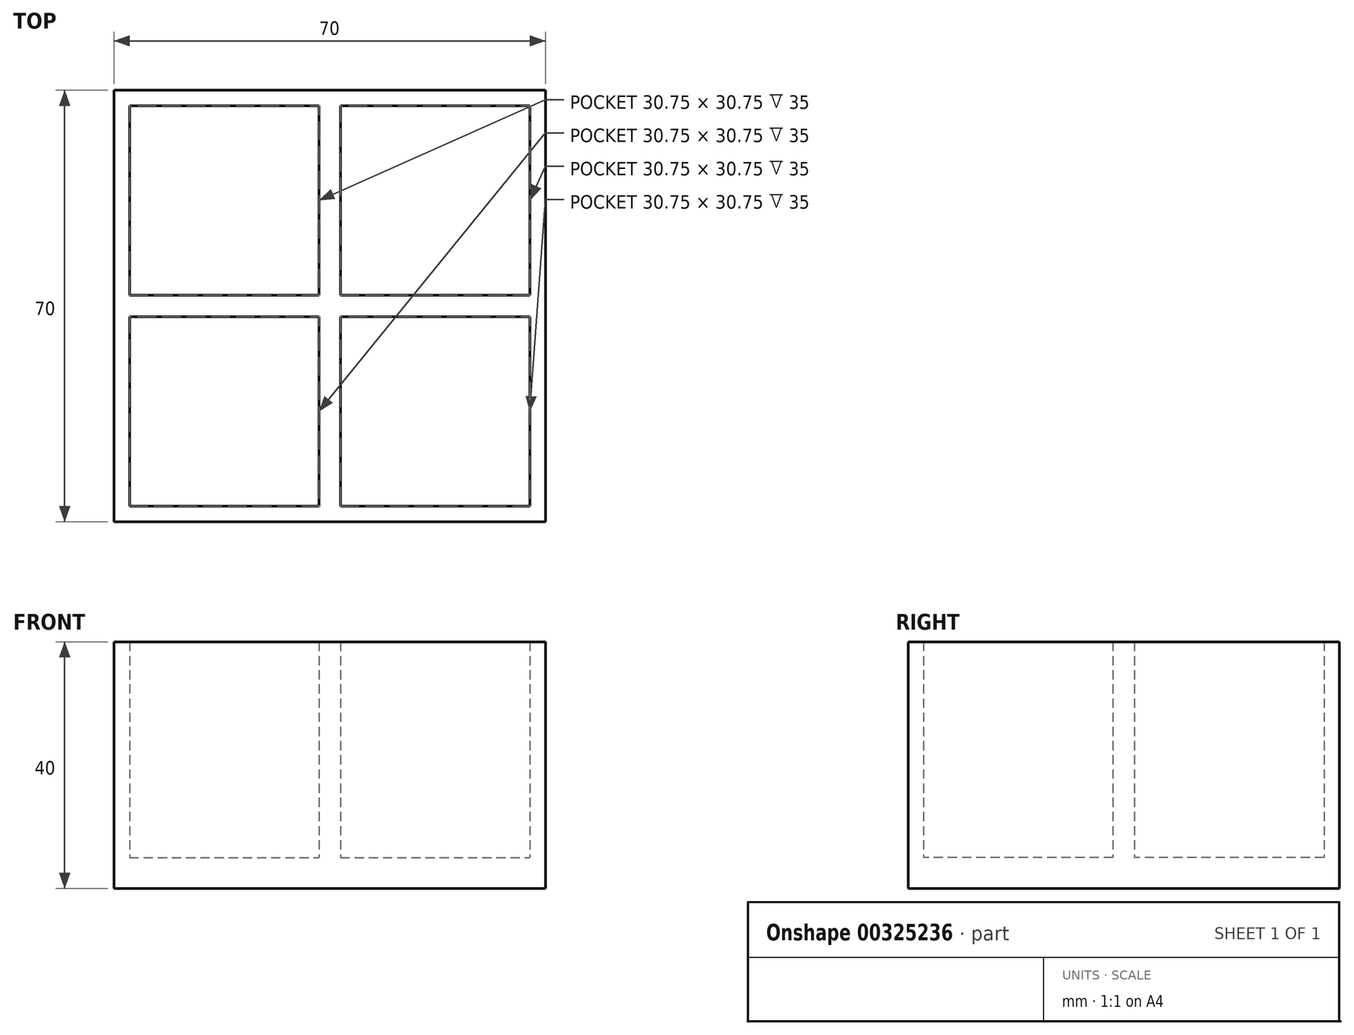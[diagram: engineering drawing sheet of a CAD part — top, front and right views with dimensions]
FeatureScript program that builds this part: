
annotation { "Feature Type Name" : "Feature", "Feature Type Description" : "" }
export const myFeature = defineFeature(function(context is Context, id is Id, definition is map)
    precondition{}
    {
        {
            var Q0;
            Q0=qCreatedBy(makeId("Top.planeOp"),FACE);
            var sketch = newSketch(context, id + "F0", { "sketchPlane" : qUnion([Q0])});
            skLineSegment(sketch, "E0.bottom", {"start": v(-35, 35) * mm, "end": v(35, 35) * mm});
            skLineSegment(sketch, "E0.top", {"start": v(-35, -35) * mm, "end": v(35, -35) * mm});
            skLineSegment(sketch, "E0.left", {"start": v(-35, 35) * mm, "end": v(-35, -35) * mm});
            skLineSegment(sketch, "E0.right", {"start": v(35, 35) * mm, "end": v(35, -35) * mm});
            skPoint(sketch, "E0.middle", {"position": v(0, 0) * mm});
            skLineSegment(sketch, "E1.bottom", {"start": v(-32.5, 32.5) * mm, "end": v(-1.75, 32.5) * mm});
            skLineSegment(sketch, "E1.top", {"start": v(-32.5, -32.5) * mm, "end": v(-1.75, -32.5) * mm});
            skLineSegment(sketch, "E1.left", {"start": v(-32.5, 32.5) * mm, "end": v(-32.5, 1.75) * mm});
            skLineSegment(sketch, "E1.right", {"start": v(32.5, 32.5) * mm, "end": v(32.5, 1.75) * mm});
            skLineSegment(sketch, "E2.left", {"start": v(-1.75, 32.5) * mm, "end": v(-1.75, 1.75) * mm});
            skLineSegment(sketch, "E2.right", {"start": v(1.75, 32.5) * mm, "end": v(1.75, 1.75) * mm});
            skLineSegment(sketch, "E3.bottom", {"start": v(-32.5, 1.75) * mm, "end": v(-1.75, 1.75) * mm});
            skLineSegment(sketch, "E3.top", {"start": v(-32.5, -1.75) * mm, "end": v(-1.75, -1.75) * mm});
            skLineSegment(sketch, "E4.trimOffspring", {"start": v(-1.75, -1.75) * mm, "end": v(-1.75, -32.5) * mm});
            skLineSegment(sketch, "E5.trimOffspring", {"start": v(1.75, 1.75) * mm, "end": v(32.5, 1.75) * mm});
            skLineSegment(sketch, "E6.trimOffspring", {"start": v(1.75, -1.75) * mm, "end": v(1.75, -32.5) * mm});
            skLineSegment(sketch, "E7.trimOffspring", {"start": v(1.75, -1.75) * mm, "end": v(32.5, -1.75) * mm});
            skLineSegment(sketch, "E8.trimOffspring", {"start": v(32.5, -1.75) * mm, "end": v(32.5, -32.5) * mm});
            skLineSegment(sketch, "E9.trimOffspring", {"start": v(1.75, 32.5) * mm, "end": v(32.5, 32.5) * mm});
            skLineSegment(sketch, "E10.trimOffspring", {"start": v(-32.5, -1.75) * mm, "end": v(-32.5, -32.5) * mm});
            skLineSegment(sketch, "E11.trimOffspring", {"start": v(1.75, -32.5) * mm, "end": v(32.5, -32.5) * mm});
            skSolve(sketch);
        }
        {
            var Q0;
            Q0 = qSketchRegion(id + "F0", true);
            extrude(context, id + "F1", {"entities" : qUnion([Q0]), "depth" : 40 * mm});
        }
        {
            var Q0;
            Q0=makeQuery(id+"F0.imprint","IMPRINT",FACE,{"disambiguationData":[TD([[makeQuery(id+"F0.imprint","IMPRINT",EDGE,{"derivedFrom":sQuery(id+"F0.wireOp",EDGE,"E1.right")}),-1.0]])]});
            var Q1;
            Q1=makeQuery(id+"F0.imprint","IMPRINT",FACE,{"disambiguationData":[TD([[makeQuery(id+"F0.imprint","IMPRINT",EDGE,{"derivedFrom":sQuery(id+"F0.wireOp",EDGE,"E6.trimOffspring")}),1.0]])]});
            var Q2;
            Q2=makeQuery(id+"F0.imprint","IMPRINT",FACE,{"disambiguationData":[TD([[makeQuery(id+"F0.imprint","IMPRINT",EDGE,{"derivedFrom":sQuery(id+"F0.wireOp",EDGE,"E1.top")}),1.0]])]});
            var Q3;
            Q3=makeQuery(id+"F0.imprint","IMPRINT",FACE,{"disambiguationData":[TD([[makeQuery(id+"F0.imprint","IMPRINT",EDGE,{"derivedFrom":sQuery(id+"F0.wireOp",EDGE,"E1.bottom")}),-1.0]])]});
            extrude(context, id + "F2", {"entities" : qUnion([Q0, Q1, Q2, Q3]), "operationType" : NewBodyOperationType.ADD, "depth" : 5 * mm});
        }
    });
